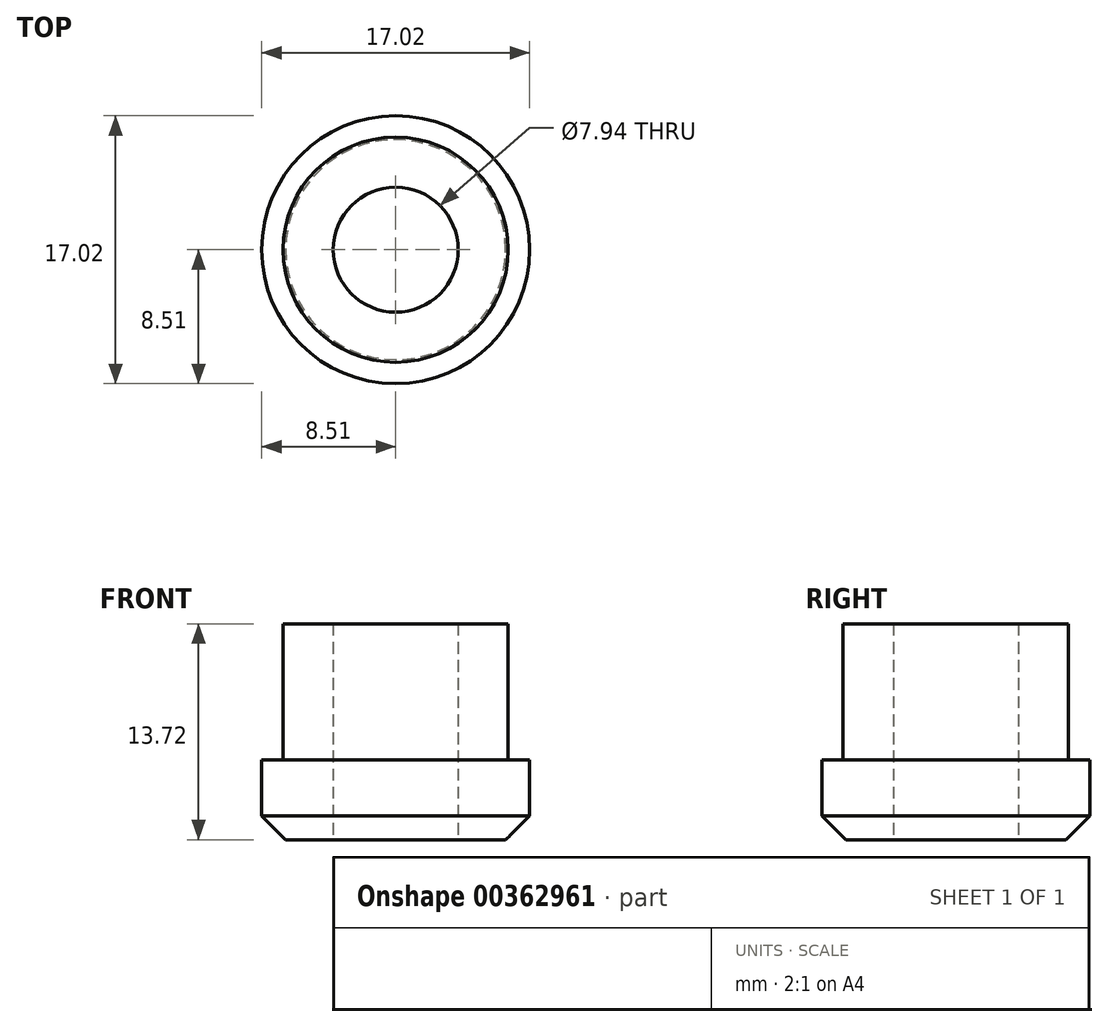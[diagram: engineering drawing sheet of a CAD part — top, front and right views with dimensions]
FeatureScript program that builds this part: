
annotation { "Feature Type Name" : "Feature", "Feature Type Description" : "" }
export const myFeature = defineFeature(function(context is Context, id is Id, definition is map)
    precondition{}
    {
        {
            var Q0;
            Q0=qCreatedBy(makeId("Top.planeOp"),FACE);
            var sketch = newSketch(context, id + "F0", { "sketchPlane" : qUnion([Q0])});
            skCircle(sketch, "E0", {"center": v(0, 0) * mm, "radius": 8.5 * mm});
            skSolve(sketch);
        }
        {
            var Q0;
            Q0=makeQuery(id+"F0.imprint","IMPRINT",FACE,{"disambiguationData":[TD([[makeQuery(id+"F0.imprint","IMPRINT",EDGE,{"derivedFrom":sQuery(id+"F0.wireOp",EDGE,"E0")}),1.0]])]});
            extrude(context, id + "F1", {"entities" : qUnion([Q0]), "depth" : 5.08 * mm});
        }
        {
            var Q0;
            Q0=makeQuery(id+"F1.opExtrude","CAP_FACE",FACE,{"disambiguationData":[OSD([sQuery(id+"F0.wireOp",EDGE,"E0")])],"isStart":false});
            var sketch = newSketch(context, id + "F2", { "sketchPlane" : qUnion([Q0])});
            skCircle(sketch, "E1", {"center": v(0, 0) * mm, "radius": 7.15 * mm});
            skSolve(sketch);
        }
        {
            var Q0;
            Q0=makeQuery(id+"F2.imprint","IMPRINT",FACE,{"disambiguationData":[TD([[makeQuery(id+"F2.imprint","IMPRINT",EDGE,{"derivedFrom":sQuery(id+"F2.wireOp",EDGE,"E1")}),1.0]])]});
            extrude(context, id + "F3", {"entities" : qUnion([Q0]), "operationType" : NewBodyOperationType.ADD, "depth" : 8.64 * mm});
        }
        {
            var Q0;
            Q0=makeQuery(id+"F1.opExtrude","CAP_FACE",FACE,{"disambiguationData":[OSD([sQuery(id+"F0.wireOp",EDGE,"E0")])],"isStart":true});
            var sketch = newSketch(context, id + "F4", { "sketchPlane" : qUnion([Q0])});
            skPoint(sketch, "E2", {"position": v(0, 0) * mm});
            skSolve(sketch);
        }
        {
            var Q0;
            Q0=sQuery(id+"F4.wireOp",VERTEX,"E2");
            var Q1;
            Q1=makeQuery(id+"F1.opExtrude","SWEPT_BODY",BODY,{"disambiguationData":[OSD([sQuery(id+"F0.wireOp",EDGE,"E0")])]});
            hole(context, id + "F5", {"style" : HoleStyle.SIMPLE, "endStyle" : HoleEndStyle.THROUGH, "holeDiameter" : 7.94 * mm, "isTappedThrough" : true, "tappedDepth" : 6.35 * mm, "tapClearance" : 3, "startFromSketch" : true, "locations" : qUnion([Q0]), "scope" : qUnion([Q1])});
        }
        {
            var Q0;
            Q0=makeQuery(id+"F1.opExtrude","CAP_EDGE",EDGE,{"disambiguationData":[OSD([sQuery(id+"F0.wireOp",EDGE,"E0")])],"isStart":true});
            chamfer(context, id + "F6", {"entities" : qUnion([Q0]), "chamferType" : ChamferType.OFFSET_ANGLE, "width" : 1.52 * mm, "oppositeDirection" : false, "angle" : 45 * degree, "tangentPropagation" : true});
        }
    });
